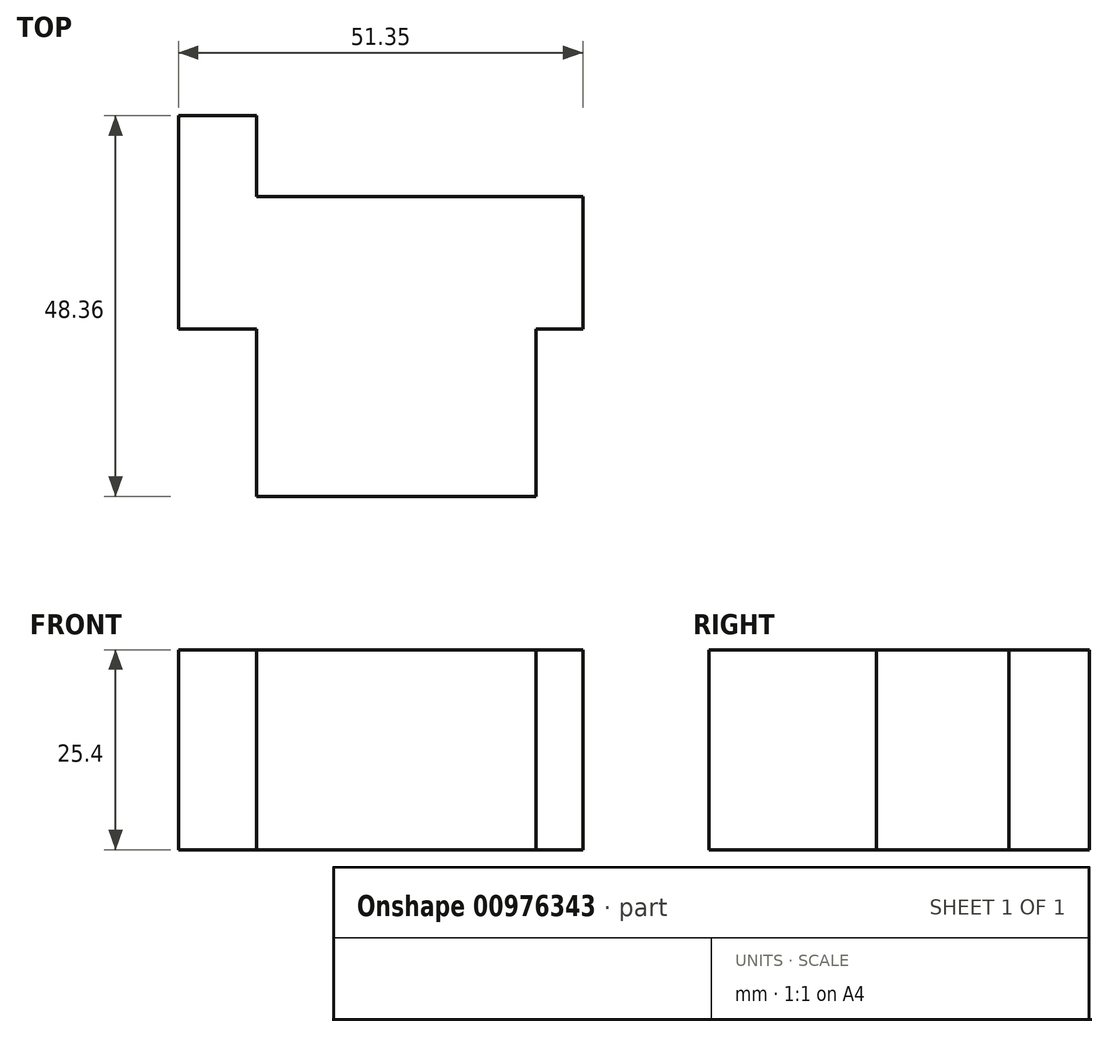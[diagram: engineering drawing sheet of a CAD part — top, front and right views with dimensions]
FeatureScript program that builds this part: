
annotation { "Feature Type Name" : "Feature", "Feature Type Description" : "" }
export const myFeature = defineFeature(function(context is Context, id is Id, definition is map)
    precondition{}
    {
        {
            var Q0;
            Q0=qCreatedBy(makeId("Top.planeOp"),FACE);
            var sketch = newSketch(context, id + "F0", { "sketchPlane" : qUnion([Q0])});
            skLineSegment(sketch, "E0.bottom", {"start": v(-26.05, 27.07) * mm, "end": v(-16.15, 27.07) * mm});
            skLineSegment(sketch, "E0.top", {"start": v(-26.05, 0) * mm, "end": v(-16.15, 0) * mm});
            skLineSegment(sketch, "E0.left", {"start": v(-26.05, 27.07) * mm, "end": v(-26.05, 0) * mm});
            skLineSegment(sketch, "E0.right", {"start": v(-16.15, 27.07) * mm, "end": v(-16.15, 0) * mm});
            skLineSegment(sketch, "E1.bottom", {"start": v(-16.15, 0) * mm, "end": v(19.33, 0) * mm});
            skLineSegment(sketch, "E1.top", {"start": v(-16.15, -21.29) * mm, "end": v(19.33, -21.29) * mm});
            skLineSegment(sketch, "E1.left", {"start": v(-16.15, 0) * mm, "end": v(-16.15, -21.29) * mm});
            skLineSegment(sketch, "E1.right", {"start": v(19.33, 0) * mm, "end": v(19.33, -21.29) * mm});
            skLineSegment(sketch, "E2.bottom", {"start": v(-16.15, 0) * mm, "end": v(25.3, 0) * mm});
            skLineSegment(sketch, "E2.top", {"start": v(-16.15, 16.8) * mm, "end": v(25.3, 16.8) * mm});
            skLineSegment(sketch, "E2.left", {"start": v(-16.15, 0) * mm, "end": v(-16.15, 16.8) * mm});
            skLineSegment(sketch, "E2.right", {"start": v(25.3, 0) * mm, "end": v(25.3, 16.8) * mm});
            skSolve(sketch);
        }
        {
            var Q0;
            Q0 = qSketchRegion(id + "F0", true);
            extrude(context, id + "F1", {"entities" : qUnion([Q0]), "depth" : 25.4 * mm, "offsetDistance" : 25.4 * mm});
        }
    });
